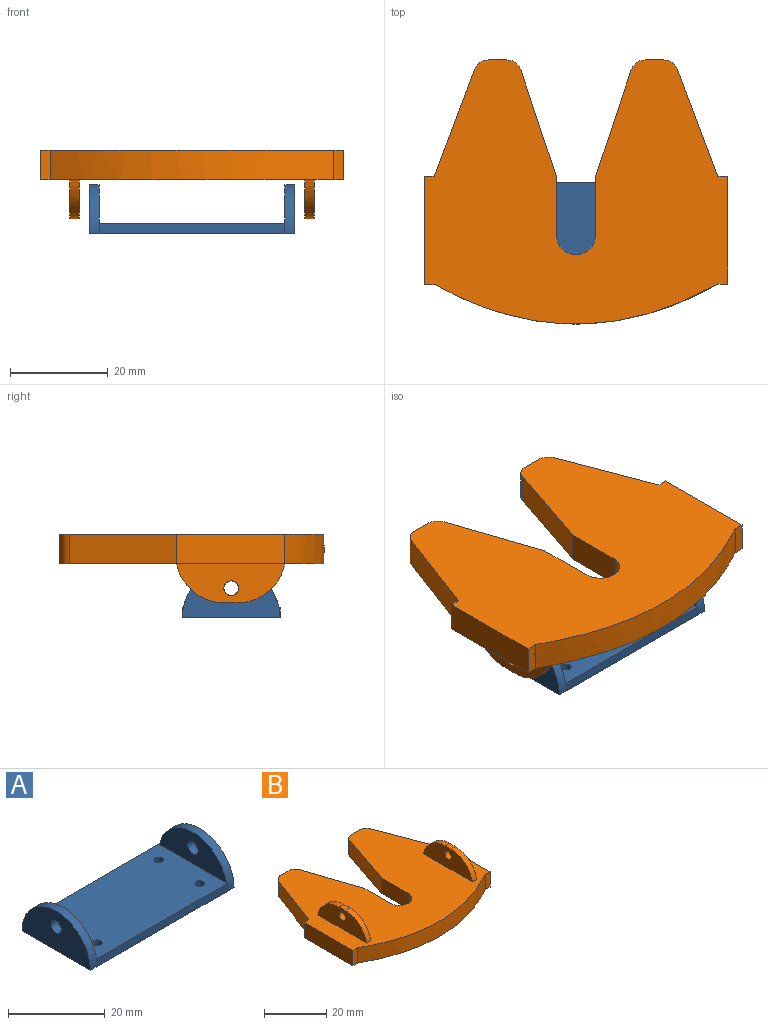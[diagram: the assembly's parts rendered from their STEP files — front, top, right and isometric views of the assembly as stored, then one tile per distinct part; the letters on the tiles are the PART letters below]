
ASSEMBLY  parts=2 mates=1
PART A: 20 faces, bbox 42x20x10 mm
  f0: plane 2x0.2mm, normal (-1,0,0), area 0.1mm2, adj f4,f6,f11
  f1: plane 2x0.2mm, normal (1,0,0), area 0.1mm2, adj f2,f6,f8
  f2: plane 38x2mm, normal (0,1,0), area 76mm2, adj f1,f3,f6,f7
  f3: plane 2x0.2mm, normal (-1,0,0), area 0.1mm2, adj f2,f6,f11
  f4: plane 38x2mm, normal (0,-1,0), area 76mm2, adj f0,f5,f6,f7
  f5: plane 2x0.2mm, normal (1,0,0), area 0.1mm2, adj f4,f6,f8
  f6: plane 38x20mm, normal (0,0,1), area 747.4mm2, adj f0,f1,f2,f3,f4,f5,f10,f13
  f7: plane 42x20mm, normal (0,0,-1), area 827.4mm2, adj f2,f4,f8,f9,f11,f12,f14,f15
  f8: cylinder r=10mm len=20mm, axis (-1,0,0), area 62.8mm2, adj f1,f5,f7,f9,f10
  f9: plane 20x10mm, normal (1,0,0), area 150mm2, adj f7,f8,f19
  f10: plane 19.6x8mm, normal (-1,0,0), area 110.3mm2, adj f6,f8,f19
  f11: cylinder r=10mm len=20mm, axis (1,0,0), area 62.8mm2, adj f0,f3,f7,f12,f13
  f12: plane 20x10mm, normal (-1,0,0), area 150mm2, adj f7,f11,f18
  f13: plane 19.6x8mm, normal (1,0,0), area 110.3mm2, adj f6,f11,f18
  f14: cylinder r=1mm len=2mm, axis (0,0,-1), area 12.6mm2, adj f6,f7
  f15: cylinder r=1mm len=2mm, axis (0,0,-1), area 12.6mm2, adj f6,f7
  f16: cylinder r=1mm len=2mm, axis (0,0,-1), area 12.6mm2, adj f6,f7
  f17: cylinder r=1mm len=2mm, axis (0,0,-1), area 12.6mm2, adj f6,f7
  f18: cylinder r=1.5mm len=3mm, axis (-1,0,0), area 18.8mm2, adj f12,f13
  f19: cylinder r=1.5mm len=3mm, axis (1,0,0), area 18.8mm2, adj f9,f10
PART B: 35 faces, bbox 62x54x14 mm
  f0: plane 62x54.02mm, normal (0,0,1), area 2253.6mm2, adj f1,f3,f4,f6,f7,f8,f9,f10
  f1: plane 6x3.77mm, normal (0,1,0), area 22.6mm2, adj f0,f5,f31,f33
  f2: plane 2.58x2mm, normal (0,0,1), area 5.1mm2, adj f3,f4,f10,f11
  f3: cylinder r=10mm len=9.8mm, axis (-1,0,0), area 27.4mm2, adj f0,f2,f10,f11
  f4: cylinder r=10mm len=9.8mm, axis (1,0,0), area 27.4mm2, adj f0,f2,f10,f11
  f5: plane 62x54.02mm, normal (0,0,-1), area 2342.2mm2, adj f1,f6,f7,f8,f9,f12,f13,f14
  f6: plane 6x2mm, normal (0,1,0), area 12mm2, adj f0,f5,f14,f15
  f7: extruded ~58x8.17mm, area 365.6mm2, adj f0,f5,f8,f12
  f8: plane 6x2mm, normal (0,-1,0), area 12mm2, adj f0,f5,f7,f9
  f9: plane 22x6mm, normal (-1,0,0), area 132mm2, adj f0,f5,f8,f17
  f10: plane 22.17x8mm, normal (-1,0,0), area 130.9mm2, adj f0,f2,f3,f4,f29
  f11: plane 22.17x8mm, normal (1,0,0), area 130.9mm2, adj f0,f2,f3,f4,f29
  f12: plane 6x0.17mm, normal (-1,0,0), area 1mm2, adj f0,f5,f7,f13
  f13: plane 6x2mm, normal (0,-1,0), area 12mm2, adj f0,f5,f12,f14
  f14: plane 22.17x6mm, normal (1,0,0), area 133mm2, adj f0,f5,f6,f13
  f15: plane 21.89x8.27mm, normal (0.94,0.35,0), area 140.4mm2, adj f0,f5,f6,f31
  f16: plane 6x3.77mm, normal (0,1,0), area 22.6mm2, adj f0,f5,f32,f34
  f17: plane 6x2mm, normal (0,1,0), area 12mm2, adj f0,f5,f9,f18
  f18: plane 21.89x8.27mm, normal (-0.94,0.35,0), area 140.4mm2, adj f0,f5,f17,f32
  f19: plane 12x6mm, normal (-1,0,0), area 72mm2, adj f0,f5,f20,f22
  f20: cylinder r=4mm len=8mm, axis (0,0,1), area 75.4mm2, adj f0,f5,f19,f21
  f21: plane 12x6mm, normal (1,0,0), area 72mm2, adj f0,f5,f20,f23
  f22: plane 21.78x7.31mm, normal (-0.95,0.32,0), area 137.9mm2, adj f0,f5,f19,f33
  f23: plane 21.78x7.31mm, normal (0.95,0.32,0), area 137.9mm2, adj f0,f5,f21,f34
  f24: cylinder r=10mm len=9.8mm, axis (1,0,0), area 27.4mm2, adj f0,f26,f27,f28
  f25: cylinder r=10mm len=9.8mm, axis (1,0,0), area 27.4mm2, adj f0,f26,f27,f28
  f26: plane 2.58x2mm, normal (0,0,1), area 5.1mm2, adj f24,f25,f27,f28
  f27: plane 22.17x8mm, normal (-1,0,0), area 130.9mm2, adj f0,f24,f25,f26,f30
  f28: plane 22.17x8mm, normal (1,0,0), area 130.9mm2, adj f0,f24,f25,f26,f30
  f29: cylinder r=1.5mm len=3mm, axis (1,0,0), area 18.8mm2, adj f10,f11
  f30: cylinder r=1.5mm len=3mm, axis (-1,0,0), area 18.8mm2, adj f27,f28
  f31: cylinder r=3mm len=6mm, axis (0,0,1), area 21.8mm2, adj f0,f1,f5,f15
  f32: cylinder r=3mm len=6mm, axis (0,0,-1), area 21.8mm2, adj f0,f5,f16,f18
  f33: cylinder r=3mm len=6mm, axis (0,0,1), area 22.4mm2, adj f0,f1,f5,f22
  f34: cylinder r=3mm len=6mm, axis (0,0,-1), area 22.4mm2, adj f0,f5,f16,f23
PLACE A at identity fixed
PLACE B rot(axis=(0,1,0),180deg) t=(21,18.01,17)mm
MATE revolute A.f18 <-> B.f29  axis (1,0,0) through (42,10,6)mm
